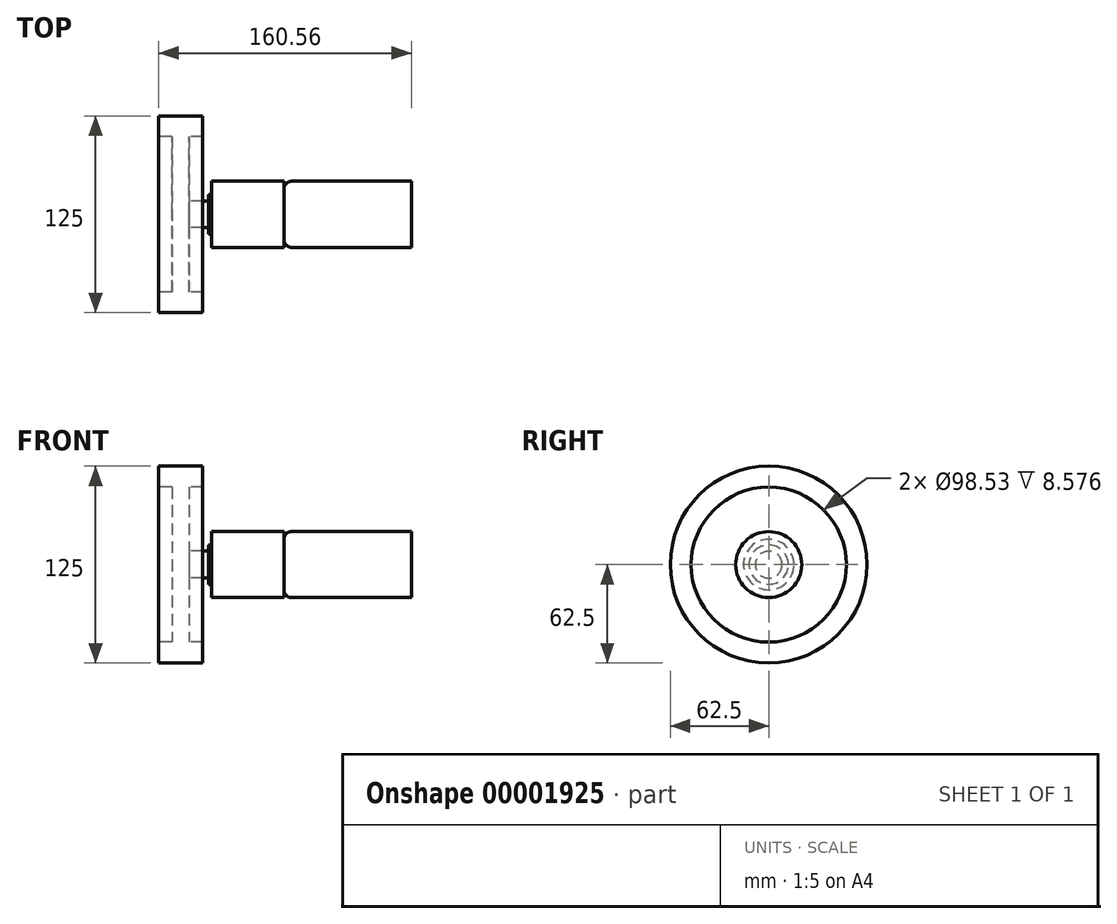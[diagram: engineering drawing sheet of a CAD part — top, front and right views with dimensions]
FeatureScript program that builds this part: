
annotation { "Feature Type Name" : "Feature", "Feature Type Description" : "" }
export const myFeature = defineFeature(function(context is Context, id is Id, definition is map)
    precondition{}
    {
        {
            var Q0;
            Q0=qCreatedBy(makeId("Top.planeOp"),FACE);
            var sketch = newSketch(context, id + "F0", { "sketchPlane" : qUnion([Q0])});
            skLineSegment(sketch, "E0.bottom", {"start": v(-2, 12.5) * mm, "end": v(0, 12.5) * mm});
            skLineSegment(sketch, "E0.top", {"start": v(-2, -12.5) * mm, "end": v(0, -12.5) * mm});
            skLineSegment(sketch, "E0.left", {"start": v(-2, 12.5) * mm, "end": v(-2, -12.5) * mm});
            skLineSegment(sketch, "E0.right", {"start": v(0, 12.5) * mm, "end": v(0, -12.5) * mm});
            skLineSegment(sketch, "E1.bottom", {"start": v(-2, 4) * mm, "end": v(-22, 4) * mm});
            skLineSegment(sketch, "E1.top", {"start": v(-2, -4) * mm, "end": v(-22, -4) * mm});
            skLineSegment(sketch, "E1.left", {"start": v(-2, 4) * mm, "end": v(-2, -4) * mm});
            skLineSegment(sketch, "E1.right", {"start": v(-22, 4) * mm, "end": v(-22, -4) * mm});
            skPoint(sketch, "E2", {"position": v(-22, 0) * mm});
            skLineSegment(sketch, "E3.bottom", {"start": v(0, 21) * mm, "end": v(45.9, 21) * mm});
            skLineSegment(sketch, "E3.top", {"start": v(0, -21) * mm, "end": v(45.9, -21) * mm});
            skLineSegment(sketch, "E3.left", {"start": v(0, 21) * mm, "end": v(0, -21) * mm});
            skLineSegment(sketch, "E3.right", {"start": v(45.9, 21) * mm, "end": v(45.9, -21) * mm});
            skLineSegment(sketch, "E4.bottom", {"start": v(50.9, 21) * mm, "end": v(111.9, 21) * mm});
            skLineSegment(sketch, "E4.top", {"start": v(50.9, -21) * mm, "end": v(111.9, -21) * mm});
            skLineSegment(sketch, "E4.left", {"start": v(45.9, 16) * mm, "end": v(45.9, -16) * mm});
            skLineSegment(sketch, "E4.right", {"start": v(111.9, 21) * mm, "end": v(111.9, -21) * mm});
            skPoint(sketch, "E5", {"position": v(111.9, 0) * mm});
            skPoint(sketch, "E6.visualSharp", {"position": v(45.9, 21) * mm});
            skArc(sketch, "E6.filletArc", {"start": v(50.9, 21) * mm, "mid": v(47.36, 19.54) * mm, "end": v(45.9, 16) * mm});
            skPoint(sketch, "E7.visualSharp", {"position": v(45.9, -21) * mm});
            skArc(sketch, "E7.filletArc", {"start": v(45.9, -16) * mm, "mid": v(47.36, -19.54) * mm, "end": v(50.9, -21) * mm});
            skLineSegment(sketch, "E8.bottom", {"start": v(111.9, 21) * mm, "end": v(126.9, 21) * mm});
            skLineSegment(sketch, "E8.top", {"start": v(111.9, -21) * mm, "end": v(126.9, -21) * mm});
            skLineSegment(sketch, "E8.right", {"start": v(126.9, 21) * mm, "end": v(126.9, -21) * mm});
            skLineSegment(sketch, "E9", {"start": v(-48.28, 0) * mm, "end": v(130.32, 0) * mm});
            skSolve(sketch);
        }
        {
            var Q0;
            {var subQ5=sQuery(id+"F0.wireOp",EDGE,"E1.bottom");Q0=makeQuery(id+"F0.imprint","IMPRINT",FACE,{"disambiguationData":[TD([[makeQuery(id+"F0.imprint","IMPRINT",EDGE,{"derivedFrom":subQ5}),1.0]])]});}
            var Q1;
            {var subQ5=sQuery(id+"F0.wireOp",EDGE,"E4.bottom");Q1=makeQuery(id+"F0.imprint","IMPRINT",FACE,{"disambiguationData":[TD([[makeQuery(id+"F0.imprint","IMPRINT",EDGE,{"derivedFrom":subQ5}),-1.0]])]});}
            var Q2;
            {var subQ7=sQuery(id+"F0.wireOp",EDGE,"E3.bottom");Q2=makeQuery(id+"F0.imprint","IMPRINT",FACE,{"disambiguationData":[TD([[makeQuery(id+"F0.imprint","IMPRINT",EDGE,{"derivedFrom":subQ7}),-1.0]])]});}
            var Q3;
            {var subQ5=sQuery(id+"F0.wireOp",EDGE,"E0.bottom");Q3=makeQuery(id+"F0.imprint","IMPRINT",FACE,{"disambiguationData":[TD([[makeQuery(id+"F0.imprint","IMPRINT",EDGE,{"derivedFrom":subQ5}),-1.0]])]});}
            var Q4;
            Q4=sQuery(id+"F0.wireOp",EDGE,"E9");
            revolve(context, id + "F1", {"entities" : qUnion([Q0, Q1, Q2, Q3]), "axis" : qUnion([Q4]), "revolveType" : RevolveType.FULL});
        }
        {
            var Q0;
            {var subQ5=sQuery(id+"F0.wireOp",EDGE,"E8.bottom");Q0=makeQuery(id+"F0.imprint","IMPRINT",FACE,{"disambiguationData":[TD([[makeQuery(id+"F0.imprint","IMPRINT",EDGE,{"derivedFrom":subQ5}),-1.0]])]});}
            var Q1;
            Q1=sQuery(id+"F0.wireOp",EDGE,"E9");
            revolve(context, id + "F2", {"operationType" : NewBodyOperationType.ADD, "entities" : qUnion([Q0]), "axis" : qUnion([Q1]), "revolveType" : RevolveType.FULL});
        }
        {
            var Q0;
            Q0=qCreatedBy(makeId("Top.planeOp"),FACE);
            var sketch = newSketch(context, id + "F3", { "sketchPlane" : qUnion([Q0])});
            skLineSegment(sketch, "E10.bottom", {"start": v(-25.08, 49.26) * mm, "end": v(-14.23, 49.26) * mm});
            skLineSegment(sketch, "E10.top", {"start": v(-25.08, -49.26) * mm, "end": v(-14.23, -49.26) * mm});
            skLineSegment(sketch, "E10.left", {"start": v(-25.08, 49.26) * mm, "end": v(-25.08, -49.26) * mm});
            skLineSegment(sketch, "E10.right", {"start": v(-14.23, 49.26) * mm, "end": v(-14.23, -49.26) * mm});
            skLineSegment(sketch, "E11.bottom", {"start": v(-14.23, 8.54) * mm, "end": v(-2, 8.54) * mm});
            skLineSegment(sketch, "E11.top", {"start": v(-14.23, -8.54) * mm, "end": v(-2, -8.54) * mm});
            skLineSegment(sketch, "E11.left", {"start": v(-14.23, 8.54) * mm, "end": v(-14.23, -8.54) * mm});
            skLineSegment(sketch, "E11.right", {"start": v(-2, 8.54) * mm, "end": v(-2, -8.54) * mm});
            skLineSegment(sketch, "E12.bottom", {"start": v(-33.66, -49.26) * mm, "end": v(-5.66, -49.26) * mm});
            skLineSegment(sketch, "E12.top", {"start": v(-33.66, -62.5) * mm, "end": v(-5.66, -62.5) * mm});
            skLineSegment(sketch, "E12.left", {"start": v(-33.66, -49.26) * mm, "end": v(-33.66, -62.5) * mm});
            skLineSegment(sketch, "E12.right", {"start": v(-5.66, -49.26) * mm, "end": v(-5.66, -62.5) * mm});
            skLineSegment(sketch, "E13.bottom", {"start": v(-33.66, 49.26) * mm, "end": v(-5.66, 49.26) * mm});
            skLineSegment(sketch, "E13.top", {"start": v(-33.66, 62.5) * mm, "end": v(-5.66, 62.5) * mm});
            skLineSegment(sketch, "E13.left", {"start": v(-33.66, 49.26) * mm, "end": v(-33.66, 62.5) * mm});
            skLineSegment(sketch, "E13.right", {"start": v(-5.66, 49.26) * mm, "end": v(-5.66, 62.5) * mm});
            skPoint(sketch, "E14", {"position": v(-25.08, 0) * mm});
            skPoint(sketch, "E15", {"position": v(-2, 0) * mm});
            skPoint(sketch, "E16", {"position": v(-19.66, -49.26) * mm});
            skLineSegment(sketch, "E17", {"start": v(-25.08, 0) * mm, "end": v(-2, 0) * mm});
            skSolve(sketch);
        }
        {
            var Q0;
            {var subQ3=sQuery(id+"F3.wireOp",EDGE,"E10.left");var subQ5=sQuery(id+"F3.wireOp",EDGE,"E13.bottom");var subQ8=makeQuery(id+"F3.imprint","INTERSECT",VERTEX,{"derivedFrom":[subQ3,subQ5]});Q0=makeQuery(id+"F3.imprint","IMPRINT",FACE,{"disambiguationData":[TD([[makeQuery(id+"F3.imprint","IMPRINT",EDGE,{"disambiguationData":[TD([[subQ8,-1.0]])],"derivedFrom":subQ3}),1.0]])]});}
            var Q1;
            Q1=makeQuery(id+"F3.imprint","IMPRINT",FACE,{"disambiguationData":[TD([[makeQuery(id+"F3.imprint","IMPRINT",EDGE,{"derivedFrom":sQuery(id+"F3.wireOp",EDGE,"E13.top")}),-1.0]])]});
            var Q2;
            {var subQ5=sQuery(id+"F3.wireOp",EDGE,"E11.bottom");Q2=makeQuery(id+"F3.imprint","IMPRINT",FACE,{"disambiguationData":[TD([[makeQuery(id+"F3.imprint","IMPRINT",EDGE,{"derivedFrom":subQ5}),-1.0]])]});}
            var Q3;
            Q3=sQuery(id+"F0.wireOp",EDGE,"E9");
            revolve(context, id + "F4", {"operationType" : NewBodyOperationType.ADD, "entities" : qUnion([Q0, Q1, Q2]), "axis" : qUnion([Q3]), "revolveType" : RevolveType.FULL});
        }
    });
